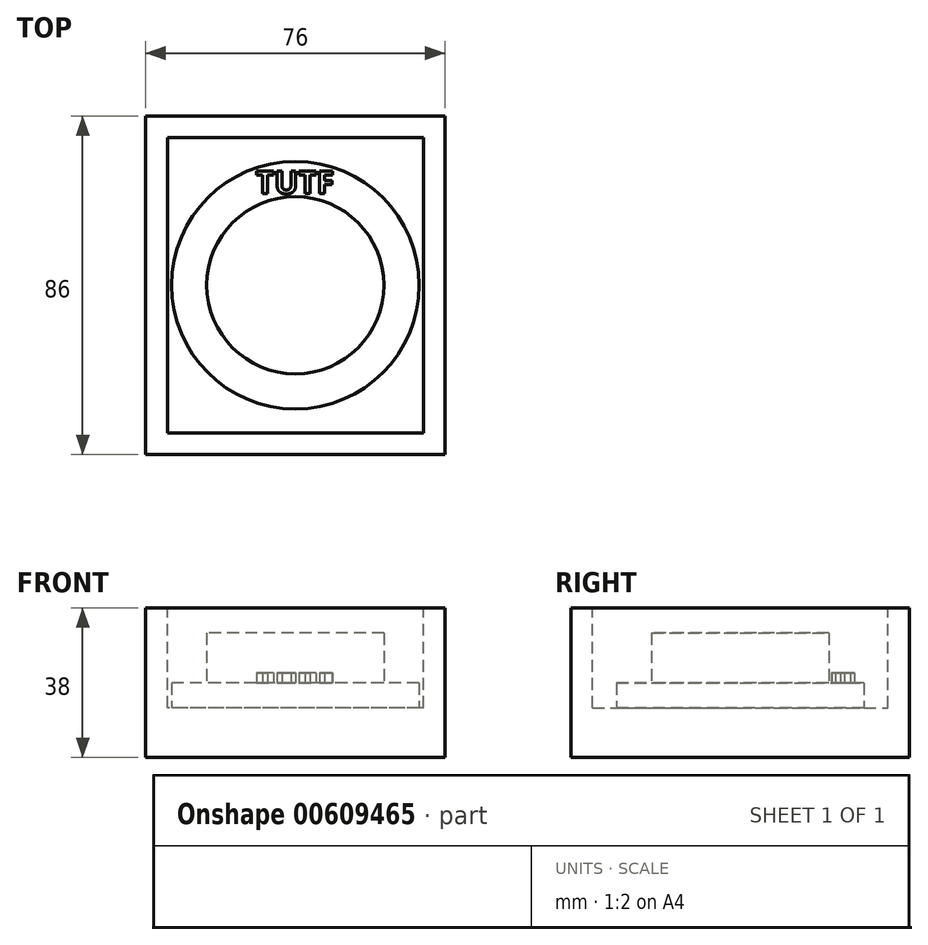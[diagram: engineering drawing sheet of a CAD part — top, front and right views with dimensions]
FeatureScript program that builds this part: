
annotation { "Feature Type Name" : "Feature", "Feature Type Description" : "" }
export const myFeature = defineFeature(function(context is Context, id is Id, definition is map)
    precondition{}
    {
        {
            var Q0;
            Q0=qCreatedBy(makeId("Top.planeOp"),FACE);
            var sketch = newSketch(context, id + "F0", { "sketchPlane" : qUnion([Q0])});
            skLineSegment(sketch, "E0.bottom", {"start": v(38, -43) * mm, "end": v(-38, -43) * mm});
            skLineSegment(sketch, "E0.top", {"start": v(38, 43) * mm, "end": v(-38, 43) * mm});
            skLineSegment(sketch, "E0.left", {"start": v(38, -43) * mm, "end": v(38, 43) * mm});
            skLineSegment(sketch, "E0.right", {"start": v(-38, -43) * mm, "end": v(-38, 43) * mm});
            skPoint(sketch, "E0.middle", {"position": v(0, 0) * mm});
            skSolve(sketch);
        }
        {
            var Q0;
            Q0 = qSketchRegion(id + "F0", true);
            extrude(context, id + "F1", {"entities" : qUnion([Q0]), "depth" : 38 * mm, "offsetDistance" : 25.4 * mm});
        }
        {
            var Q0;
            Q0=makeQuery(id+"F1.opExtrude","CAP_FACE",FACE,{"disambiguationData":[OSD([sQuery(id+"F0.wireOp",EDGE,"E0.bottom"),sQuery(id+"F0.wireOp",EDGE,"E0.top"),sQuery(id+"F0.wireOp",EDGE,"E0.left"),sQuery(id+"F0.wireOp",EDGE,"E0.right")])],"isStart":false});
            var sketch = newSketch(context, id + "F2", { "sketchPlane" : qUnion([Q0])});
            skLineSegment(sketch, "E1.bottom", {"start": v(32.5, -37.5) * mm, "end": v(-32.5, -37.5) * mm});
            skLineSegment(sketch, "E1.top", {"start": v(32.5, 37.5) * mm, "end": v(-32.5, 37.5) * mm});
            skLineSegment(sketch, "E1.left", {"start": v(32.5, -37.5) * mm, "end": v(32.5, 37.5) * mm});
            skLineSegment(sketch, "E1.right", {"start": v(-32.5, -37.5) * mm, "end": v(-32.5, 37.5) * mm});
            skPoint(sketch, "E1.middle", {"position": v(0, 0) * mm});
            skSolve(sketch);
        }
        {
            var Q0;
            Q0 = qSketchRegion(id + "F2", true);
            extrude(context, id + "F3", {"entities" : qUnion([Q0]), "operationType" : NewBodyOperationType.REMOVE, "oppositeDirection" : true, "depth" : 25.4 * mm, "offsetDistance" : 25.4 * mm});
        }
        {
            var Q0;
            Q0=makeQuery(id+"F3.boolean.opBoolean","COPY",FACE,{"derivedFrom":makeQuery(id+"F3.opExtrude","CAP_FACE",FACE,{"disambiguationData":[OSD([sQuery(id+"F2.wireOp",EDGE,"E1.bottom"),sQuery(id+"F2.wireOp",EDGE,"E1.top"),sQuery(id+"F2.wireOp",EDGE,"E1.left"),sQuery(id+"F2.wireOp",EDGE,"E1.right")])],"isStart":false})});
            var sketch = newSketch(context, id + "F4", { "sketchPlane" : qUnion([Q0])});
            skCircle(sketch, "E2", {"center": v(0, 0) * mm, "radius": 31.43 * mm});
            skSolve(sketch);
        }
        {
            var Q0;
            Q0 = qSketchRegion(id + "F4", true);
            extrude(context, id + "F5", {"entities" : qUnion([Q0]), "operationType" : NewBodyOperationType.ADD, "depth" : 6.35 * mm, "offsetDistance" : 25.4 * mm});
        }
        {
            var Q0;
            Q0=makeQuery(id+"F5.opExtrude","CAP_FACE",FACE,{"disambiguationData":[OSD([sQuery(id+"F4.wireOp",EDGE,"E2")])],"isStart":false});
            var sketch = newSketch(context, id + "F6", { "sketchPlane" : qUnion([Q0])});
            skCircle(sketch, "E3", {"center": v(0, 0) * mm, "radius": 22.5 * mm});
            skSolve(sketch);
        }
        {
            var Q0;
            Q0 = qSketchRegion(id + "F6", true);
            extrude(context, id + "F7", {"entities" : qUnion([Q0]), "operationType" : NewBodyOperationType.ADD, "depth" : 12.7 * mm, "offsetDistance" : 25.4 * mm});
        }
        {
            var Q0;
            Q0=makeQuery(id+"F5.opExtrude","CAP_FACE",FACE,{"disambiguationData":[OSD([sQuery(id+"F4.wireOp",EDGE,"E2")])],"isStart":false});
            var sketch = newSketch(context, id + "F8", { "sketchPlane" : qUnion([Q0])});
            skCircle(sketch, "E4", {"center": v(0, 0) * mm, "radius": 25.04 * mm});
            skCircle(sketch, "E5", {"center": v(0, 0) * mm, "radius": 31 * mm});
            skSolve(sketch);
        }
        {
            var Q0;
            Q0=makeQuery(id+"F8.imprint","IMPRINT",FACE,{"disambiguationData":[TD([[makeQuery(id+"F8.imprint","IMPRINT",EDGE,{"derivedFrom":sQuery(id+"F8.wireOp",EDGE,"E4")}),-1.0]])]});
            var sketch = newSketch(context, id + "F9", { "sketchPlane" : qUnion([Q0])});
            skText(sketch, "E6", { "text": "TUTF", "fontName": "NotoSans-Bold.ttf"});
            const initialGuessF9  = {"E6": [-0.01, 0.02327, 1, 0, 0.00581]};
            skSetInitialGuess(sketch, initialGuessF9);
            skSolve(sketch);
        }
        {
            var Q0;
            Q0 = qSketchRegion(id + "F9", true);
            extrude(context, id + "F10", {"entities" : qUnion([Q0]), "operationType" : NewBodyOperationType.ADD, "depth" : 2.54 * mm, "offsetDistance" : 25.4 * mm});
        }
    });
